# Revit family: Villeroy_Boch-Hommage_Washdown_WC-3D
name_source: partatom
category: Plumbing Fixtures
units: mm (PartAtom-declared; Revit-internal decimal feet)

## family parameters
Always vertical = Yes
Cut with Voids When Loaded = No
Part Type = Normal
Room Calculation Point = No
Round Connector Dimension = Use Diameter
Shared = No
Work Plane-Based = No

## types (1)
- Villeroy_Boch-Hommage_Washdown_WC-3D
    Default Elevation = 0 cm
    Description = Un design innovant à l'élégance intemporelle et à la qualité exceptionnelle :  voilà ce que garantit Villeroy & Boch et ce depuis 1748. En se basant sur cette tradition, les designers et chefs de produit ont développé des collections et des concepts afin de créer des cadres de vie.
    Manufacturer = Villeroy & Boch
    Model = Villeroy Boch Hommage Washdown WC
    Type Comments = Que ce soit dans les domaines de la salle de bains et wellness, l'art de la table, les carrelages ou la cuisine, nos produits se distinguent par leur impression d'élégance, leur maniabilité intuitive et leur qualité à long terme. Laissez-vous surprendre et convaincre par notre design innovant made by Villeroy & Boch.
    URL = http://www.villeroy-boch.fr
    Villeroy & Boch AG Matériau = Céramique

## geometry (parser evidence)
native form markers: Blend x4, Sweep x4
no freeform markers — native parametric forms only
